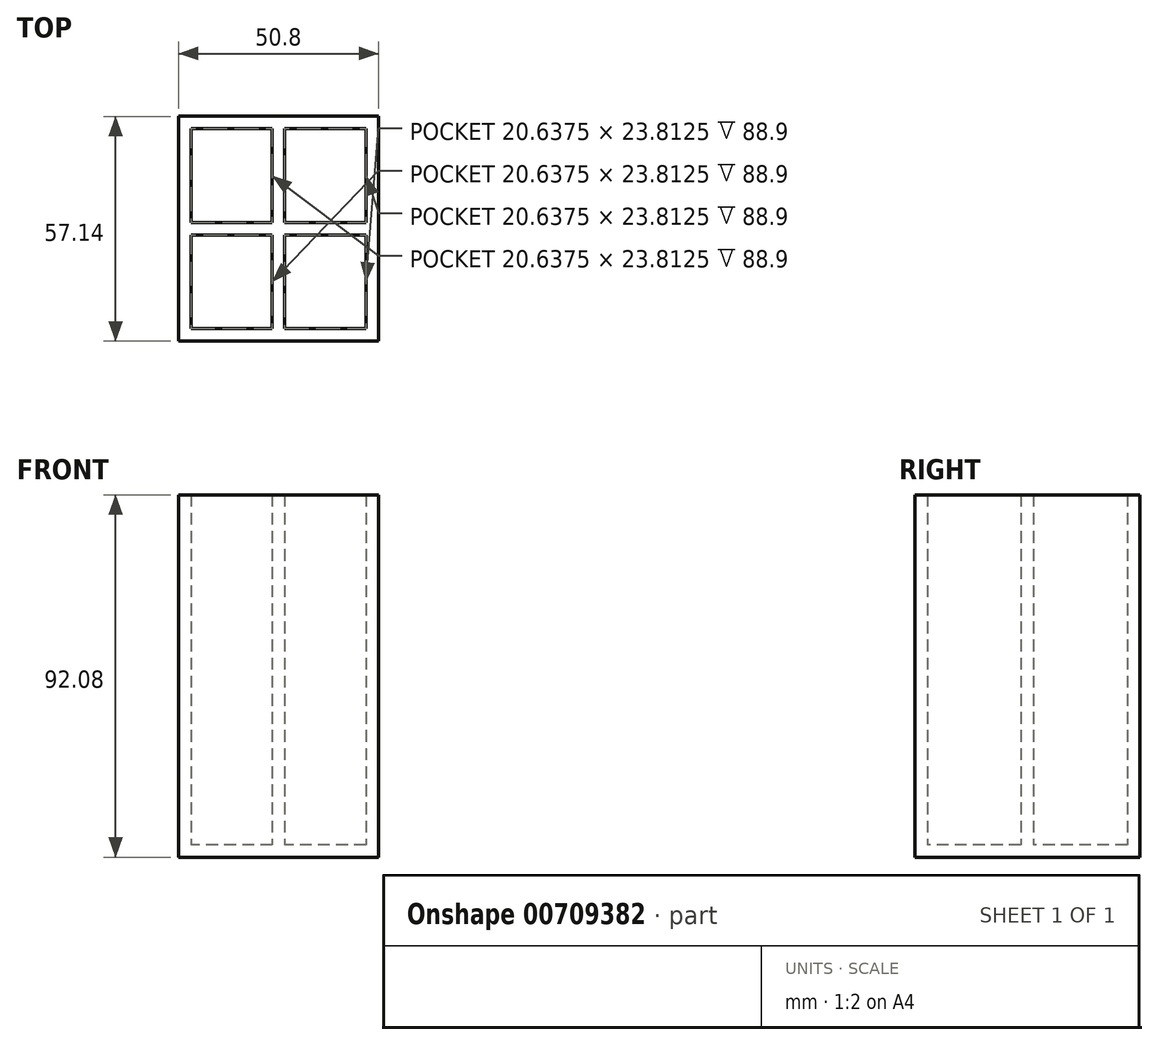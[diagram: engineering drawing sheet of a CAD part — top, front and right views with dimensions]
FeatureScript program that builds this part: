
annotation { "Feature Type Name" : "Feature", "Feature Type Description" : "" }
export const myFeature = defineFeature(function(context is Context, id is Id, definition is map)
    precondition{}
    {
        {
            var Q0;
            Q0=qCreatedBy(makeId("Top.planeOp"),FACE);
            var sketch = newSketch(context, id + "F0", { "sketchPlane" : qUnion([Q0])});
            skLineSegment(sketch, "E0.bottom", {"start": v(25.4, 28.58) * mm, "end": v(-25.4, 28.58) * mm});
            skLineSegment(sketch, "E0.top", {"start": v(25.4, -28.57) * mm, "end": v(-25.4, -28.57) * mm});
            skLineSegment(sketch, "E0.left", {"start": v(25.4, 28.57) * mm, "end": v(25.4, -28.58) * mm});
            skLineSegment(sketch, "E0.right", {"start": v(-25.4, 28.58) * mm, "end": v(-25.4, -28.57) * mm});
            skPoint(sketch, "E0.middle", {"position": v(0, 0) * mm});
            skSolve(sketch);
        }
        {
            var Q0;
            Q0 = qSketchRegion(id + "F0", true);
            extrude(context, id + "F1", {"entities" : qUnion([Q0]), "depth" : 3.17 * mm, "offsetDistance" : 25.4 * mm});
        }
        {
            var Q0;
            Q0=makeQuery(id+"F1.opExtrude","CAP_FACE",FACE,{"disambiguationData":[OSD([sQuery(id+"F0.wireOp",EDGE,"E0.bottom"),sQuery(id+"F0.wireOp",EDGE,"E0.top"),sQuery(id+"F0.wireOp",EDGE,"E0.left"),sQuery(id+"F0.wireOp",EDGE,"E0.right")])],"isStart":false});
            var sketch = newSketch(context, id + "F2", { "sketchPlane" : qUnion([Q0])});
            skLineSegment(sketch, "E1.bottom", {"start": v(-25.4, -25.4) * mm, "end": v(25.4, -25.4) * mm});
            skLineSegment(sketch, "E1.top", {"start": v(-25.4, -28.58) * mm, "end": v(25.4, -28.58) * mm});
            skLineSegment(sketch, "E1.left", {"start": v(-25.4, -25.4) * mm, "end": v(-25.4, -28.58) * mm});
            skLineSegment(sketch, "E1.right", {"start": v(25.4, -25.4) * mm, "end": v(25.4, -28.58) * mm});
            skSolve(sketch);
        }
        {
            var Q0;
            Q0=makeQuery(id+"F2.imprint","IMPRINT",FACE,{"disambiguationData":[TD([[makeQuery(id+"F2.imprint","IMPRINT",EDGE,{"derivedFrom":sQuery(id+"F2.wireOp",EDGE,"E1.bottom")}),-1.0]])]});
            extrude(context, id + "F3", {"entities" : qUnion([Q0]), "operationType" : NewBodyOperationType.ADD, "depth" : 88.9 * mm, "offsetDistance" : 25.4 * mm});
        }
        {
            var Q0;
            Q0=makeQuery(id+"F1.opExtrude","CAP_FACE",FACE,{"disambiguationData":[OSD([sQuery(id+"F0.wireOp",EDGE,"E0.bottom"),sQuery(id+"F0.wireOp",EDGE,"E0.top"),sQuery(id+"F0.wireOp",EDGE,"E0.left"),sQuery(id+"F0.wireOp",EDGE,"E0.right")])],"isStart":false});
            var sketch = newSketch(context, id + "F4", { "sketchPlane" : qUnion([Q0])});
            skLineSegment(sketch, "E2.bottom", {"start": v(-25.4, 28.58) * mm, "end": v(25.4, 28.58) * mm});
            skLineSegment(sketch, "E2.top", {"start": v(-25.4, 25.4) * mm, "end": v(25.4, 25.4) * mm});
            skLineSegment(sketch, "E2.left", {"start": v(-25.4, 28.58) * mm, "end": v(-25.4, 25.4) * mm});
            skLineSegment(sketch, "E2.right", {"start": v(25.4, 28.58) * mm, "end": v(25.4, 25.4) * mm});
            skSolve(sketch);
        }
        {
            var Q0;
            Q0=makeQuery(id+"F4.imprint","IMPRINT",FACE,{"disambiguationData":[TD([[makeQuery(id+"F4.imprint","IMPRINT",EDGE,{"derivedFrom":sQuery(id+"F4.wireOp",EDGE,"E2.bottom")}),1.0]])]});
            extrude(context, id + "F5", {"entities" : qUnion([Q0]), "operationType" : NewBodyOperationType.ADD, "depth" : 88.9 * mm, "offsetDistance" : 25.4 * mm});
        }
        {
            var Q0;
            Q0=makeQuery(id+"F1.opExtrude","CAP_FACE",FACE,{"disambiguationData":[OSD([sQuery(id+"F0.wireOp",EDGE,"E0.bottom"),sQuery(id+"F0.wireOp",EDGE,"E0.top"),sQuery(id+"F0.wireOp",EDGE,"E0.left"),sQuery(id+"F0.wireOp",EDGE,"E0.right")])],"isStart":false});
            var sketch = newSketch(context, id + "F6", { "sketchPlane" : qUnion([Q0])});
            skLineSegment(sketch, "E3.bottom", {"start": v(-25.4, 25.4) * mm, "end": v(-22.22, 25.4) * mm});
            skLineSegment(sketch, "E3.top", {"start": v(-25.4, -25.4) * mm, "end": v(-22.22, -25.4) * mm});
            skLineSegment(sketch, "E3.left", {"start": v(-25.4, 25.4) * mm, "end": v(-25.4, -25.4) * mm});
            skLineSegment(sketch, "E3.right", {"start": v(-22.22, 25.4) * mm, "end": v(-22.22, -25.4) * mm});
            skSolve(sketch);
        }
        {
            var Q0;
            Q0=makeQuery(id+"F6.imprint","IMPRINT",FACE,{"disambiguationData":[TD([[makeQuery(id+"F6.imprint","IMPRINT",EDGE,{"derivedFrom":sQuery(id+"F6.wireOp",EDGE,"E3.bottom")}),-1.0]])]});
            extrude(context, id + "F7", {"entities" : qUnion([Q0]), "operationType" : NewBodyOperationType.ADD, "depth" : 88.9 * mm, "offsetDistance" : 25.4 * mm});
        }
        {
            var Q0;
            Q0=makeQuery(id+"F1.opExtrude","CAP_FACE",FACE,{"disambiguationData":[OSD([sQuery(id+"F0.wireOp",EDGE,"E0.bottom"),sQuery(id+"F0.wireOp",EDGE,"E0.top"),sQuery(id+"F0.wireOp",EDGE,"E0.left"),sQuery(id+"F0.wireOp",EDGE,"E0.right")])],"isStart":false});
            var sketch = newSketch(context, id + "F8", { "sketchPlane" : qUnion([Q0])});
            skLineSegment(sketch, "E4.bottom", {"start": v(25.4, 25.4) * mm, "end": v(22.23, 25.4) * mm});
            skLineSegment(sketch, "E4.top", {"start": v(25.4, -25.4) * mm, "end": v(22.23, -25.4) * mm});
            skLineSegment(sketch, "E4.left", {"start": v(25.4, 25.4) * mm, "end": v(25.4, -25.4) * mm});
            skLineSegment(sketch, "E4.right", {"start": v(22.23, 25.4) * mm, "end": v(22.23, -25.4) * mm});
            skSolve(sketch);
        }
        {
            var Q0;
            Q0=makeQuery(id+"F8.imprint","IMPRINT",FACE,{"disambiguationData":[TD([[makeQuery(id+"F8.imprint","IMPRINT",EDGE,{"derivedFrom":sQuery(id+"F8.wireOp",EDGE,"E4.bottom")}),-1.0]])]});
            extrude(context, id + "F9", {"entities" : qUnion([Q0]), "operationType" : NewBodyOperationType.ADD, "depth" : 88.9 * mm, "offsetDistance" : 25.4 * mm});
        }
        {
            var Q0;
            Q0=makeQuery(id+"F1.opExtrude","CAP_FACE",FACE,{"disambiguationData":[OSD([sQuery(id+"F0.wireOp",EDGE,"E0.bottom"),sQuery(id+"F0.wireOp",EDGE,"E0.top"),sQuery(id+"F0.wireOp",EDGE,"E0.left"),sQuery(id+"F0.wireOp",EDGE,"E0.right")])],"isStart":false});
            var sketch = newSketch(context, id + "F10", { "sketchPlane" : qUnion([Q0])});
            skLineSegment(sketch, "E5.bottom", {"start": v(1.59, 25.4) * mm, "end": v(-1.59, 25.4) * mm});
            skLineSegment(sketch, "E5.top", {"start": v(1.59, -25.4) * mm, "end": v(-1.59, -25.4) * mm});
            skLineSegment(sketch, "E5.left", {"start": v(1.59, 25.4) * mm, "end": v(1.59, -25.4) * mm});
            skLineSegment(sketch, "E5.right", {"start": v(-1.59, 25.4) * mm, "end": v(-1.59, -25.4) * mm});
            skPoint(sketch, "E5.middle", {"position": v(0, 0) * mm});
            skSolve(sketch);
        }
        {
            var Q0;
            Q0=makeQuery(id+"F10.imprint","IMPRINT",FACE,{"disambiguationData":[TD([[makeQuery(id+"F10.imprint","IMPRINT",EDGE,{"derivedFrom":sQuery(id+"F10.wireOp",EDGE,"E5.bottom")}),-1.0]])]});
            extrude(context, id + "F11", {"entities" : qUnion([Q0]), "operationType" : NewBodyOperationType.ADD, "depth" : 88.9 * mm, "offsetDistance" : 25.4 * mm});
        }
        {
            var Q0;
            Q0=makeQuery(id+"F11.boolean.opBoolean","SPLIT",FACE,{"disambiguationData":[TD([makeQuery(id+"F9.opExtrude","SWEPT_FACE",FACE,{"disambiguationData":[OSD([sQuery(id+"F8.wireOp",EDGE,"E4.right")])]})])],"derivedFrom":makeQuery(id+"F1.opExtrude","CAP_FACE",FACE,{"disambiguationData":[OSD([sQuery(id+"F0.wireOp",EDGE,"E0.bottom"),sQuery(id+"F0.wireOp",EDGE,"E0.top"),sQuery(id+"F0.wireOp",EDGE,"E0.left"),sQuery(id+"F0.wireOp",EDGE,"E0.right")])],"isStart":false})});
            var sketch = newSketch(context, id + "F12", { "sketchPlane" : qUnion([Q0])});
            skLineSegment(sketch, "E6.bottom", {"start": v(22.23, 1.59) * mm, "end": v(-22.23, 1.59) * mm});
            skLineSegment(sketch, "E6.top", {"start": v(22.23, -1.59) * mm, "end": v(-22.23, -1.59) * mm});
            skLineSegment(sketch, "E6.left", {"start": v(22.23, 1.59) * mm, "end": v(22.23, -1.59) * mm});
            skLineSegment(sketch, "E6.right", {"start": v(-22.23, 1.59) * mm, "end": v(-22.23, -1.59) * mm});
            skPoint(sketch, "E6.middle", {"position": v(0, 0) * mm});
            skSolve(sketch);
        }
        {
            var Q0;
            {var subQ0=sQuery(id+"F12.wireOp",EDGE,"E6.right");Q0=makeQuery(id+"F12.imprint","IMPRINT",FACE,{"disambiguationData":[TD([[makeQuery(id+"F12.imprint","IMPRINT",EDGE,{"derivedFrom":subQ0}),1.0]])]});}
            var Q1;
            {var subQ0=sQuery(id+"F12.wireOp",EDGE,"E6.left");Q1=makeQuery(id+"F12.imprint","IMPRINT",FACE,{"disambiguationData":[TD([[makeQuery(id+"F12.imprint","IMPRINT",EDGE,{"derivedFrom":subQ0}),-1.0]])]});}
            extrude(context, id + "F13", {"entities" : qUnion([Q0, Q1]), "operationType" : NewBodyOperationType.ADD, "depth" : 88.9 * mm, "offsetDistance" : 25.4 * mm});
        }
    });
